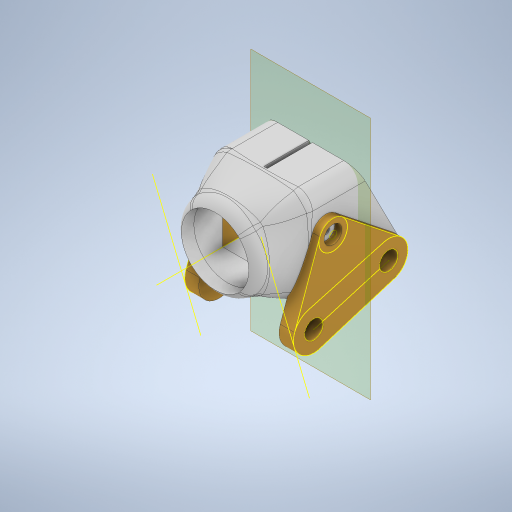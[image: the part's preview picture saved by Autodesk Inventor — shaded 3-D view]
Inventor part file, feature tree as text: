
AUTODESK INVENTOR PART (.ipt)
format: ipt  version: 2023 (Build 270158000, 158)  size: 1,092,608 bytes
history: native  units: in
note: dims shown in document units (in); Inventor stores cm internally (conversion verified against a paired STEP export)
features: sketch x9, projected_geometry x7, extrude x6, other x4, fillet x1, plane x1, chamfer x1
ambient origin geometry x8: Origin, YZ Plane, XZ Plane, XY Plane, X Axis, Y Axis, Z Axis, Center Point
bodies: Solid1 (feature_tree)
feature tree (29):
  other  "mini predator camera block for boolian.iam"
  other  "mini predator camera block.ipt:1"
  other  "Kauri modular camera mount mini.ipt:1"
  other  "adjustable camera mount mirror.ipt:1"
  extrude  "Extrusion1"  Depth=0.3937in TaperAngle=0.0deg
  extrude  "Extrusion2"  Depth=1.0in TaperAngle=0.0deg
  extrude  "Extrusion3"  TaperAngle=90.0deg  [1 undecoded]
  fillet  "Fillet1"  Radius=0.0197in
  plane  "Work Plane1"
  extrude  "Extrusion4"  Depth=0.1in TaperAngle=0.0deg
  extrude  "Extrusion5"  Depth=0.1in TaperAngle=0.0deg
  extrude  "Extrusion6"  [1 undecoded]
  chamfer  "Chamfer1"  [1 undecoded]
  sketch  "Sketch18"
  sketch  "Sketch2"  dims[d3=1.0in d4=0.0in d5=1.0in d6=0.0in]
  sketch  "Sketch2_1"  dims[d0=0.3937in d1=1.0in d2=0.0in]
  sketch  "Sketch4"  dims[d7=0.125in d8=90.0deg d9=0.0197in]
  projected_geometry  "Projected Loop1"
  projected_geometry  "Projected Loop2"
  sketch  "Sketch5"  dims[d10=0.5in d11=0.0in d12=0.1in d13=0.0in]
  sketch  "Sketch6"  dims[d14=180.0deg d15=0.1in d16=0.0in]
  projected_geometry  "Projected Loop3"
  projected_geometry  "Projected Loop4"
  sketch  "Sketch7"  dims[d17=0.0787in d18=0.125in d19=45.0deg]
  sketch  "Sketch8"
  projected_geometry  "Projected Loop5"
  projected_geometry  "Projected Loop6"
  sketch  "Sketch9"
  projected_geometry  "Projected Loop7"
note: 3 required parameter values undecoded (feature->parameter linkage not recoverable at this tier; creation-order binding heuristic only, values carry confidence <= 0.55)
